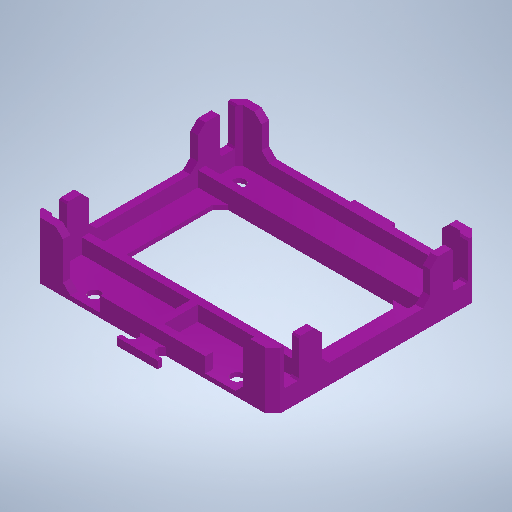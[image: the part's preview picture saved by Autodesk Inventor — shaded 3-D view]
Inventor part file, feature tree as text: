
AUTODESK INVENTOR PART (.ipt)
format: ipt  version: 2025.3 (Build 293356000, 356)  size: 528,896 bytes
history: native  units: mm
features: extrude x7, chamfer x6, sketch x3, other x1
ambient origin geometry x8: Origin, YZ Plane, XZ Plane, XY Plane, X Axis, Y Axis, Z Axis, Center Point
bodies: Body1 (feature_tree)
feature tree (17):
  other  "ソリッド1"
  sketch  "スケッチ1"
  extrude  "ベース"  Depth=17.5mm
  extrude  "壁"  Depth=62.5mm
  extrude  "補強"  Depth=51.0mm
  extrude  "輪ゴムフック1"  Depth=38.0mm
  extrude  "輪ゴムフック2"  Depth=9.0mm
  chamfer  "面取り1"  Distance=51.0mm
  chamfer  "面取り4"  Distance=3.2mm
  chamfer  "面取り5"  Distance=2.0mm
  chamfer  "面取り6"  Distance=2.0mm
  extrude  "コード取り出し溝"  Depth=11.0mm
  chamfer  "面取り7"  Distance=11.0mm
  chamfer  "面取り8"  Distance=6.0mm
  extrude  "押し出し8"  TaperAngle=0.0deg  [1 undecoded]
  sketch  "スケッチ2"
  sketch  "スケッチ3"
note: 1 required parameter value undecoded (feature->parameter linkage not recoverable at this tier; creation-order binding heuristic only, values carry confidence <= 0.55)
